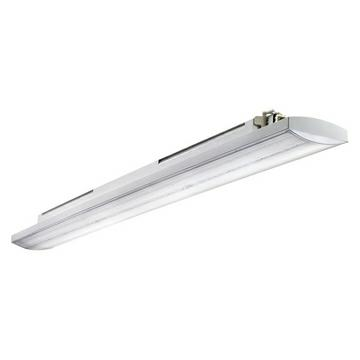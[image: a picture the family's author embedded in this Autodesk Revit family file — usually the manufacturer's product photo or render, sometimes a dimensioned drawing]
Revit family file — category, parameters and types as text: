
# Revit family: Lighting-Industrial-GEWISS-SMART[3]PLUS-WATERTIGHT-LED_TRANSPARENT_800mm
name_source: partatom
category: Apparecchi per illuminazione
units: mm (PartAtom-declared; Revit-internal decimal feet)

## family parameters
Condiviso = No
Host = Superficie
Punto di calcolo locali = No
Quota connettore circolare = Usa diametro
Sorgente d'illuminazione = Sì
Taglio con vuoti quando caricato = No
Tipo di parte = Normale

## types (1)
- Lighting-Industrial-GEWISS-SMART[3]PLUS-WATERTIGHT-LED_TRANSPARENT_800mm
    Angolo inclinazione = -90.00°
    Application = Indoor
    Carico apparente = 35 VA
    Catalogue = LIGHTING
    Catalogue Range = SMART[3] PLUS
    Colour temperature = 5700 K (CRI > 90)
    Colour temperature: = 5700 K (CRI > 90)
    Commenti sul wattaggio = 35W
    D_simbolo = 129 mm
    Descrizione = SMART3 PLUS 800 T.W.DALI HE TRASP 9 57
    Efficiency class of integrated LEDs = A ÷ A++
    Electrocod = 2434
    Emetti da lunghezza linea = 700 mm  [stored 2.29659 ft]
    File diagramma fotometrico = GWS3123AT957.IES
    Filtro dei colori = 16777215
    Ganci = GEWISS  - ALLUMINIO
    Glow Wire Test = 850°C
    IDF = d9498619-7e87-423a-8f78-a261baa5849d
    IDT = a7a40100-d365-495d-870d-5573c78dcb86
    IP degree = IP66/IP69
    Immagine tipo = GWS3236TC.jpg
    Insulation class = II
    Lamp = LED
    Lampada = LED
    Length = 800 mm
    Lumen output (lm) = 3100
    Lunghezza Lampada = 800 mm  [stored 2.62467 ft]
    Modello = GWS3123AT957
    Numero poli = 2
    Operating temperature: = -25 +50 °C
    Produttore = GEWISS S.p.A.
    Prospetto di default = 1219 mm
    SEO = Ceiling
    Schermo. = Gewiss - Led Acceso
    Shield type = Transparent
    Shock resistance = IK08
    Stampa 1_100 = Sì
    Stampa 1_200 = No
    Struttura = GEWISS - SMART 3 - GRIGIO
    System power = 26 W
    Technical sheet = https://www.gewiss.com
    Type of light source = LED - Not replaceable
    Typology = DALI
    URL = https://www.gewiss.com
    Variazione temperatura colore lampada con luminosità attenuata = <Nessuno>
    Version file RFA = 20.0
    Voltage = 220-240 V
    Warranty = 5 years
    Working temperature = -25 +50 °C

note: [stored X ft] marks values corroborated as IEEE doubles in the binary element streams (Revit-internal decimal feet)
